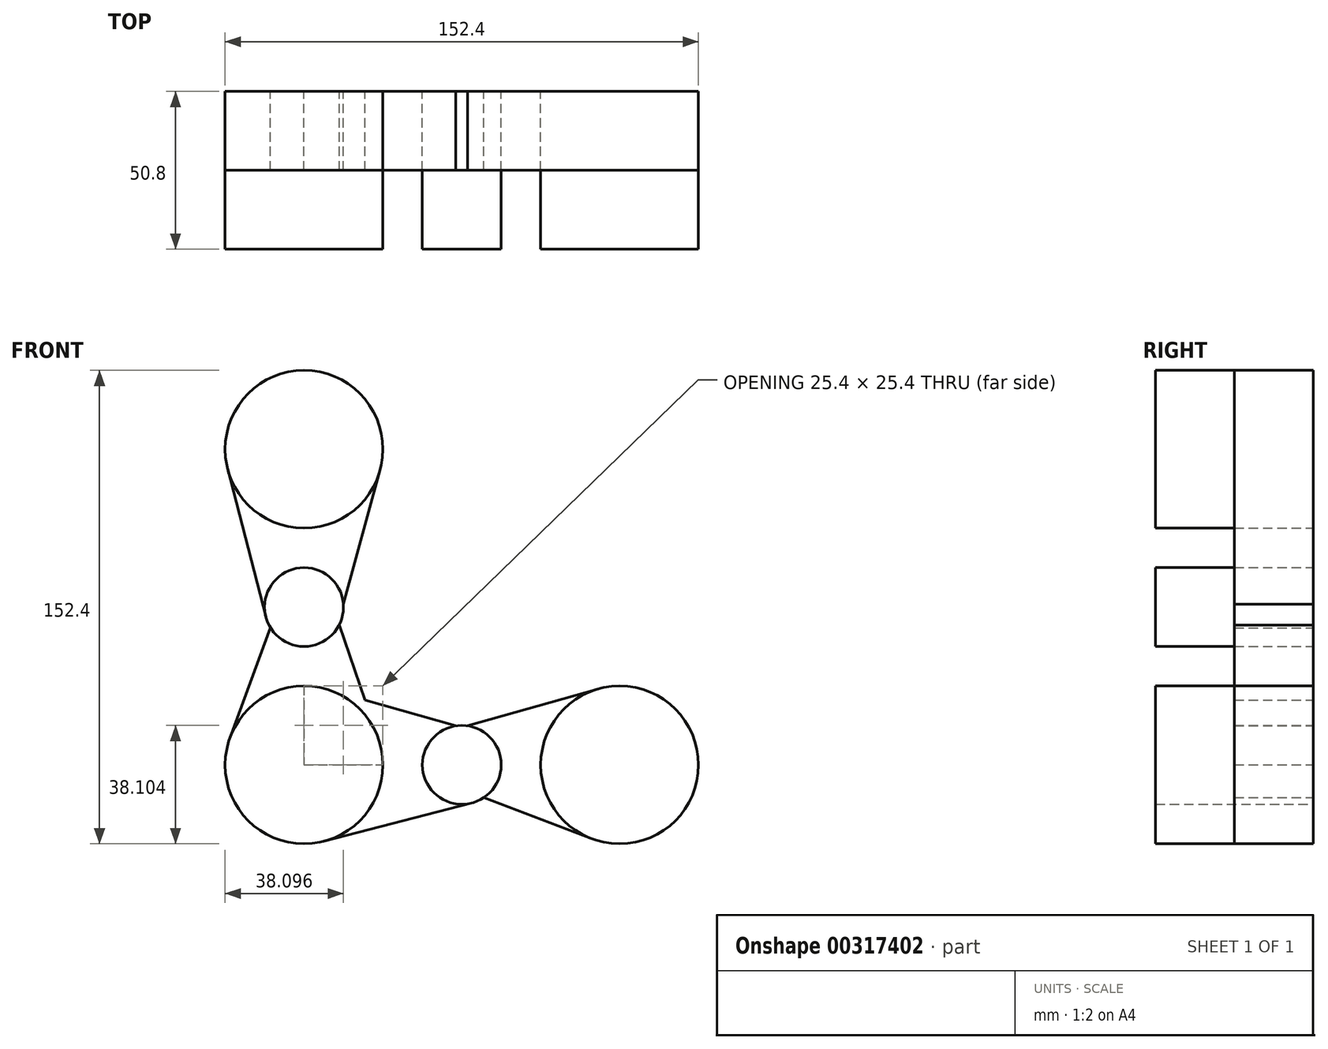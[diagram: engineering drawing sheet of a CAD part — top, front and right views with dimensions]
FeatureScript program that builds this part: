
annotation { "Feature Type Name" : "Feature", "Feature Type Description" : "" }
export const myFeature = defineFeature(function(context is Context, id is Id, definition is map)
    precondition{}
    {
        {
            var Q0;
            Q0=qCreatedBy(makeId("Front.planeOp"),FACE);
            var sketch = newSketch(context, id + "F0", { "sketchPlane" : qUnion([Q0])});
            skLineSegment(sketch, "E0", {"start": v(-113.4, 73.87) * mm, "end": v(-113.4, 23.07) * mm});
            skLineSegment(sketch, "E1", {"start": v(-113.4, 23.07) * mm, "end": v(-113.4, -27.73) * mm});
            skLineSegment(sketch, "E2", {"start": v(-113.4, -27.73) * mm, "end": v(-62.6, -27.73) * mm});
            skLineSegment(sketch, "E3", {"start": v(-62.6, -27.73) * mm, "end": v(-11.8, -27.73) * mm});
            skCircle(sketch, "E4", {"center": v(-113.4, 73.87) * mm, "radius": 25.4 * mm});
            skCircle(sketch, "E5", {"center": v(-113.4, -27.73) * mm, "radius": 25.4 * mm});
            skCircle(sketch, "E6", {"center": v(-11.8, -27.73) * mm, "radius": 25.4 * mm});
            skCircle(sketch, "E7", {"center": v(-113.4, 23.07) * mm, "radius": 12.7 * mm});
            skCircle(sketch, "E8", {"center": v(-62.6, -27.73) * mm, "radius": 12.7 * mm});
            skLineSegment(sketch, "E9", {"start": v(-137.99, 67.52) * mm, "end": v(-125.7, 19.9) * mm});
            skLineSegment(sketch, "E10", {"start": v(-124.2, 16.4) * mm, "end": v(-137.23, -18.94) * mm});
            skLineSegment(sketch, "E11", {"start": v(-107.04, -52.32) * mm, "end": v(-59.42, -40.02) * mm});
            skLineSegment(sketch, "E12", {"start": v(-20.83, -51.46) * mm, "end": v(-55.5, -38.26) * mm});
            skLineSegment(sketch, "E13", {"start": v(-88.9, 67.15) * mm, "end": v(-100.73, 24.05) * mm});
            skLineSegment(sketch, "E14", {"start": v(-89.38, -19.44) * mm, "end": v(-102.07, 17.33) * mm});
            skLineSegment(sketch, "E15", {"start": v(-106.47, -3.29) * mm, "end": v(-64.5, -15.17) * mm});
            skLineSegment(sketch, "E16", {"start": v(-18.71, -3.29) * mm, "end": v(-60.68, -15.17) * mm});
            skSolve(sketch);
        }
        {
            var Q0;
            {var subQ0=sQuery(id+"F0.wireOp",EDGE,"E4");var subQ1=makeQuery(id+"F0.imprint","INTERSECT",VERTEX,{"derivedFrom":[subQ0,sQuery(id+"F0.wireOp",EDGE,"E9")]});Q0=makeQuery(id+"F0.imprint","IMPRINT",FACE,{"disambiguationData":[TD([[makeQuery(id+"F0.imprint","IMPRINT",EDGE,{"disambiguationData":[TD([[subQ1,-1.0]])],"derivedFrom":subQ0}),1.0]])]});}
            var Q1;
            {var subQ3=sQuery(id+"F0.wireOp",EDGE,"E1");var subQ4=sQuery(id+"F0.wireOp",EDGE,"E0");var subQ5=makeQuery(id+"F0.imprint","INTERSECT",VERTEX,{"derivedFrom":[subQ4,subQ3]});Q1=makeQuery(id+"F0.imprint","IMPRINT",FACE,{"disambiguationData":[TD([[makeQuery(id+"F0.imprint","IMPRINT",EDGE,{"disambiguationData":[TD([[subQ5,1.0]])],"derivedFrom":subQ4}),-1.0]])]});}
            var Q2;
            {var subQ2=sQuery(id+"F0.wireOp",EDGE,"E0");var subQ4=sQuery(id+"F0.wireOp",EDGE,"E1");var subQ5=makeQuery(id+"F0.imprint","INTERSECT",VERTEX,{"derivedFrom":[subQ2,subQ4]});Q2=makeQuery(id+"F0.imprint","IMPRINT",FACE,{"disambiguationData":[TD([[makeQuery(id+"F0.imprint","IMPRINT",EDGE,{"disambiguationData":[TD([[subQ5,1.0]])],"derivedFrom":subQ2}),1.0]])]});}
            var Q3;
            {var subQ3=sQuery(id+"F0.wireOp",EDGE,"E1");var subQ5=sQuery(id+"F0.wireOp",EDGE,"E2");var subQ6=makeQuery(id+"F0.imprint","INTERSECT",VERTEX,{"derivedFrom":[subQ3,subQ5]});Q3=makeQuery(id+"F0.imprint","IMPRINT",FACE,{"disambiguationData":[TD([[makeQuery(id+"F0.imprint","IMPRINT",EDGE,{"disambiguationData":[TD([[subQ6,1.0]])],"derivedFrom":subQ3}),-1.0]])]});}
            var Q4;
            {var subQ2=sQuery(id+"F0.wireOp",EDGE,"E2");var subQ4=sQuery(id+"F0.wireOp",EDGE,"E1");var subQ5=makeQuery(id+"F0.imprint","INTERSECT",VERTEX,{"derivedFrom":[subQ4,subQ2]});Q4=makeQuery(id+"F0.imprint","IMPRINT",FACE,{"disambiguationData":[TD([[makeQuery(id+"F0.imprint","IMPRINT",EDGE,{"disambiguationData":[TD([[subQ5,1.0]])],"derivedFrom":subQ4}),1.0]])]});}
            var Q5;
            {var subQ3=sQuery(id+"F0.wireOp",EDGE,"E3");var subQ4=sQuery(id+"F0.wireOp",EDGE,"E2");var subQ5=makeQuery(id+"F0.imprint","INTERSECT",VERTEX,{"derivedFrom":[subQ4,subQ3]});Q5=makeQuery(id+"F0.imprint","IMPRINT",FACE,{"disambiguationData":[TD([[makeQuery(id+"F0.imprint","IMPRINT",EDGE,{"disambiguationData":[TD([[subQ5,1.0]])],"derivedFrom":subQ4}),1.0]])]});}
            var Q6;
            {var subQ2=sQuery(id+"F0.wireOp",EDGE,"E2");var subQ4=sQuery(id+"F0.wireOp",EDGE,"E3");var subQ5=makeQuery(id+"F0.imprint","INTERSECT",VERTEX,{"derivedFrom":[subQ2,subQ4]});Q6=makeQuery(id+"F0.imprint","IMPRINT",FACE,{"disambiguationData":[TD([[makeQuery(id+"F0.imprint","IMPRINT",EDGE,{"disambiguationData":[TD([[subQ5,1.0]])],"derivedFrom":subQ2}),-1.0]])]});}
            var Q7;
            {var subQ0=sQuery(id+"F0.wireOp",EDGE,"E6");var subQ1=makeQuery(id+"F0.imprint","INTERSECT",VERTEX,{"derivedFrom":[subQ0,sQuery(id+"F0.wireOp",EDGE,"E16")]});Q7=makeQuery(id+"F0.imprint","IMPRINT",FACE,{"disambiguationData":[TD([[makeQuery(id+"F0.imprint","IMPRINT",EDGE,{"disambiguationData":[TD([[subQ1,-1.0]])],"derivedFrom":subQ0}),1.0]])]});}
            extrude(context, id + "F1", {"entities" : qUnion([Q0, Q1, Q2, Q3, Q4, Q5, Q6, Q7]), "depth" : 50.8 * mm});
        }
        {
            var Q0;
            Q0 = qSketchRegion(id + "F0", true);
            extrude(context, id + "F2", {"entities" : qUnion([Q0]), "depth" : 25.4 * mm});
        }
    });
